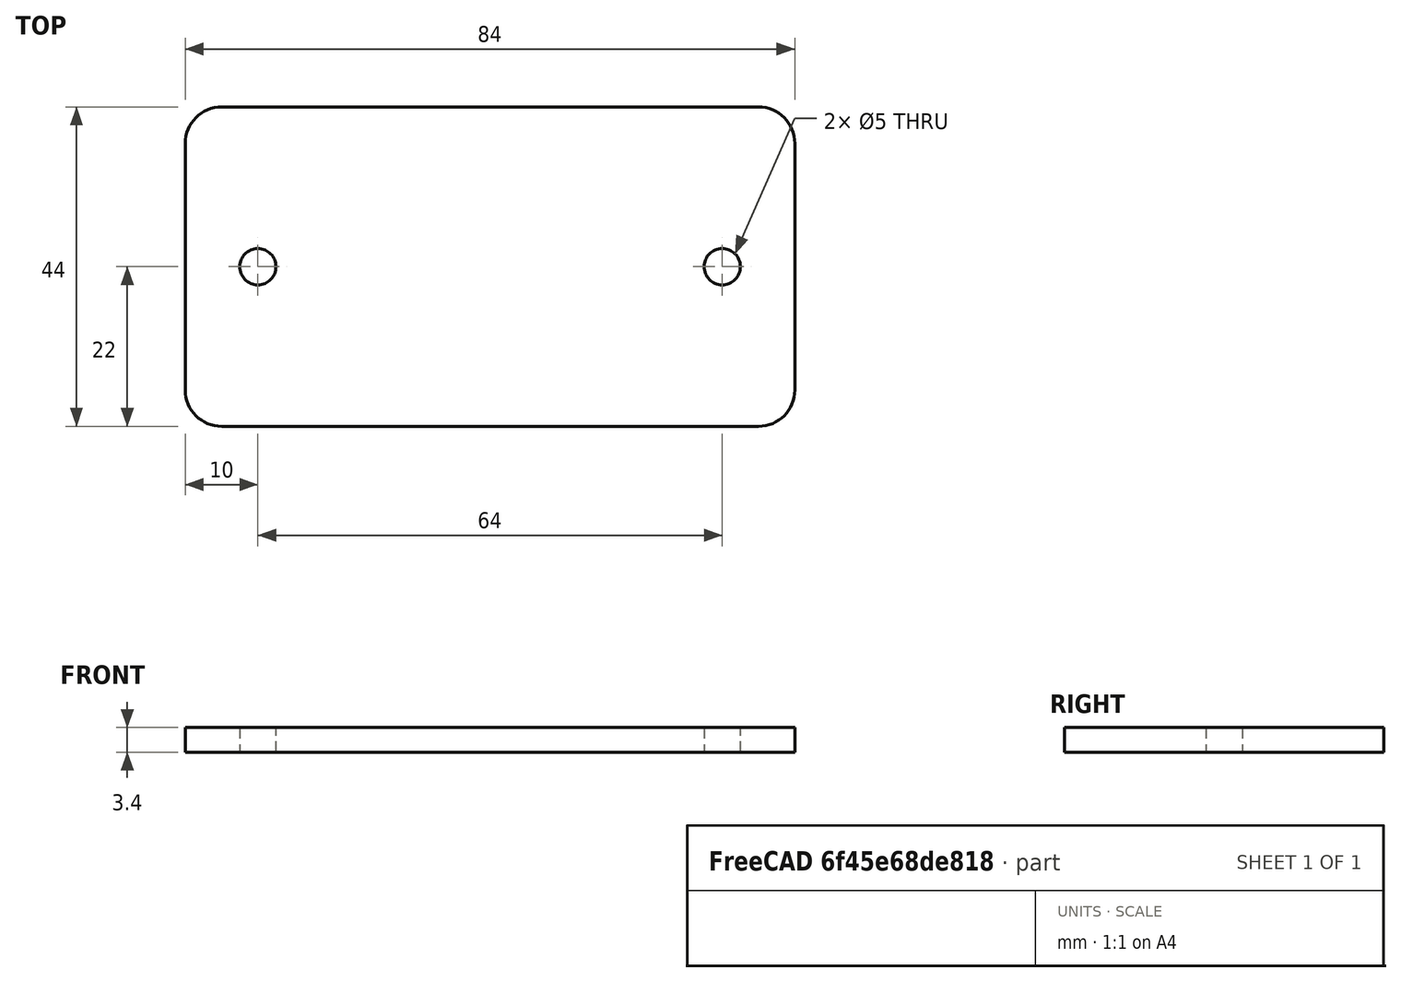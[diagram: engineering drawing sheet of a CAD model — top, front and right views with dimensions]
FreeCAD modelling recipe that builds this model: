
FCSTD DOCUMENT  (FreeCAD 1.0R39109 (Git))
Label: Unnamed
License: All rights reserved
LicenseURL: https://en.wikipedia.org/wiki/All_rights_reserved
objects: Sketcher::SketchObject×1, PartDesign::Pad×1, PartDesign::Body×1
note: 6 computed .brp shape members not serialized (recipe doc carries the construction recipe); baked Part::Feature solids carry a one-line shape summary decoded from their .brp

FEATURE [Sketcher::SketchObject] Sketch
  ArcFitTolerance = 1e-06
  AttachmentSupport = -> [XY_Plane]
  FullyConstrained = true
  MakeInternals = false
  MapMode = 5
  sketch-geometry (15):
    g0: LineSegment StartX=-42 StartY=17 StartZ=0 EndX=-42 EndY=-17 EndZ=0
    g1: LineSegment StartX=-37 StartY=-22 StartZ=0 EndX=37 EndY=-22 EndZ=0
    g2: LineSegment StartX=42 StartY=-17 StartZ=0 EndX=42 EndY=17 EndZ=0
    g3: LineSegment StartX=37 StartY=22 StartZ=0 EndX=-37 EndY=22 EndZ=0
    g4: GeomPoint [constr] X=0 Y=0 Z=0
    g5: Circle CenterX=-32 CenterY=0 CenterZ=0 NormalX=0 NormalY=0 NormalZ=1 AngleXU=0 Radius=2.5
    g6: Circle CenterX=32 CenterY=0 CenterZ=0 NormalX=0 NormalY=0 NormalZ=1 AngleXU=0 Radius=2.5
    g7: ArcOfCircle CenterX=-37 CenterY=17 CenterZ=0 NormalX=0 NormalY=0 NormalZ=1 AngleXU=0 Radius=5 StartAngle=1.5708 EndAngle=3.14159
    g8: GeomPoint [constr] X=-42 Y=22 Z=0
    g9: ArcOfCircle CenterX=-37 CenterY=-17 CenterZ=0 NormalX=0 NormalY=0 NormalZ=1 AngleXU=0 Radius=5 StartAngle=3.14159 EndAngle=4.71239
    g10: GeomPoint [constr] X=-42 Y=-22 Z=0
    g11: ArcOfCircle CenterX=37 CenterY=-17 CenterZ=0 NormalX=0 NormalY=0 NormalZ=1 AngleXU=0 Radius=5 StartAngle=4.71239 EndAngle=6.28319
    g12: GeomPoint [constr] X=42 Y=-22 Z=0
    g13: ArcOfCircle CenterX=37 CenterY=17 CenterZ=0 NormalX=0 NormalY=0 NormalZ=1 AngleXU=0 Radius=5 StartAngle=-7.1019e-12 EndAngle=1.5708
    g14: GeomPoint [constr] X=42 Y=22 Z=0
  constraints (33):
    c: Vertical(g0)
    c: Vertical(g2)
    c: Horizontal(g1)
    c: Horizontal(g3)
    c: Symmetric(g12,g8,g4)
    c: Coincident(g4,g-1)
    c: PointOnObject(g5,g-1)
    c: Equal(g6,g5)
    c: Diameter(g5) = 5
    c: DistanceX(g5,g6) = 64
    c: DistanceX(g8,g14) = 84
    c: Symmetric(g5,g6,g4)
    c: DistanceY(g10,g8) = 44
    c: PointOnObject(g8,g3)
    c: PointOnObject(g8,g0)
    c: Tangent(g3,g7) = -1.5708
    c: Tangent(g0,g7) = -1.5708
    c: PointOnObject(g10,g0)
    c: PointOnObject(g10,g1)
    c: Tangent(g0,g9) = -1.5708
    c: Tangent(g1,g9) = -1.5708
    c: PointOnObject(g12,g1)
    c: PointOnObject(g12,g2)
    c: Tangent(g1,g11) = -1.5708
    c: Tangent(g2,g11) = -1.5708
    c: PointOnObject(g14,g3)
    c: PointOnObject(g14,g2)
    c: Tangent(g3,g13) = -1.5708
    c: Tangent(g2,g13) = -1.5708
    c: Equal(g13,g11)
    c: Equal(g11,g9)
    c: Equal(g9,g7)
    c: Diameter(g7) = 10
FEATURE [PartDesign::Pad] Pad
  Direction = (0,0,1)
  Length = 3.4
  Length2 = 10
  Profile = -> Sketch
  ReferenceAxis = -> Sketch [N_Axis]
  Refine = true
  Suppressed = false
  Type = 0
FEATURE [PartDesign::Body] Body
  AllowCompound = false
  Group = -> [Sketch,Pad]
  Origin = -> Origin
  Tip = -> Pad
